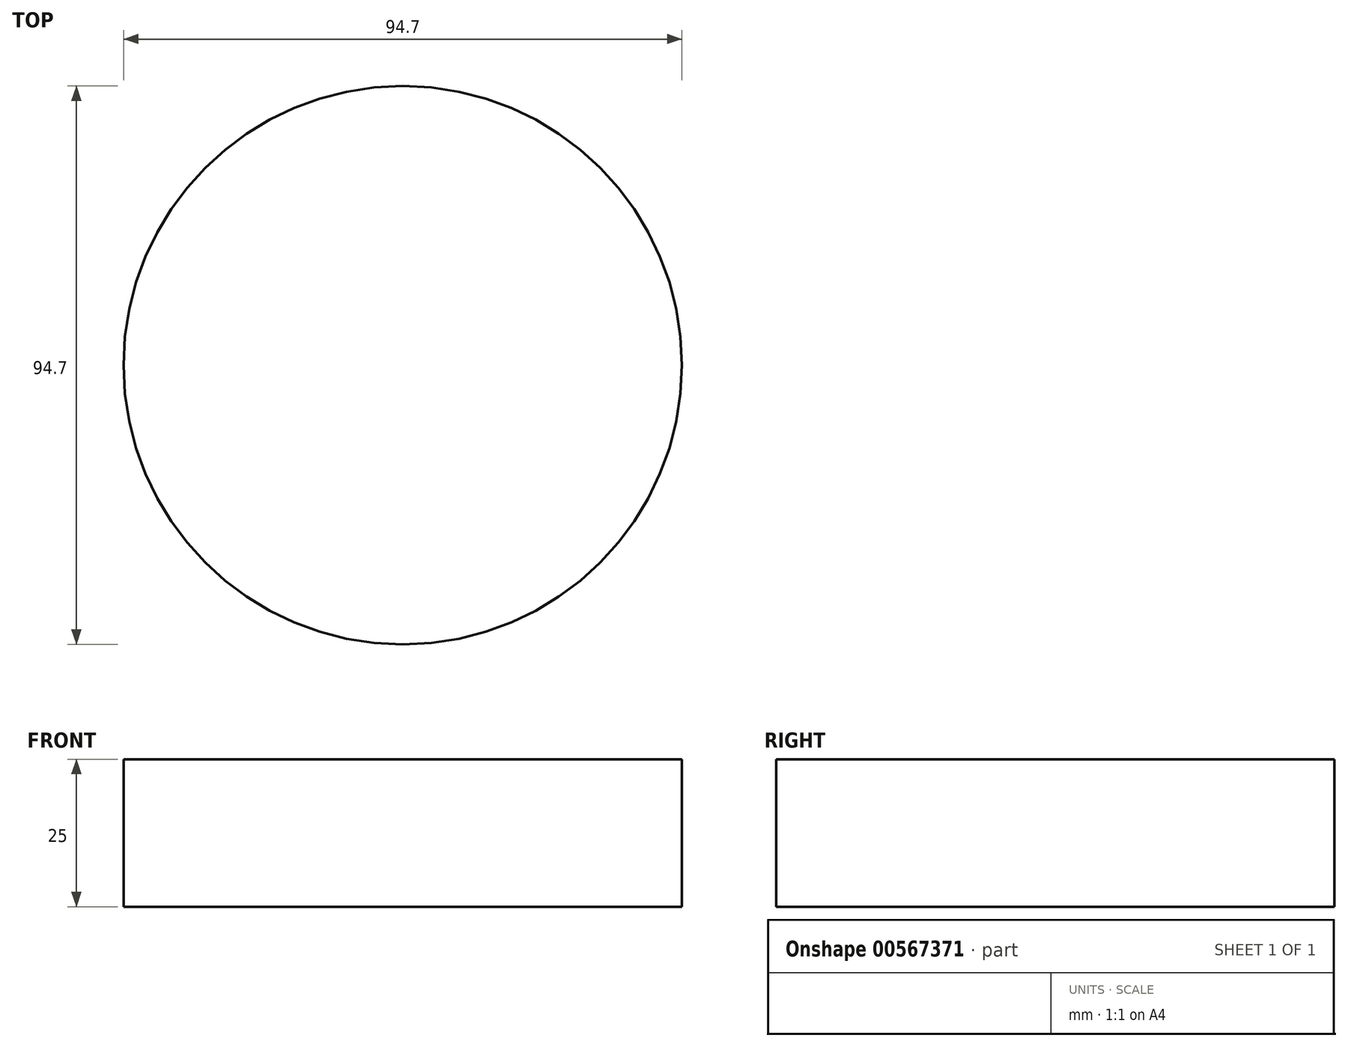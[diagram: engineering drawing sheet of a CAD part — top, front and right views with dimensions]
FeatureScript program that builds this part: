
annotation { "Feature Type Name" : "Feature", "Feature Type Description" : "" }
export const myFeature = defineFeature(function(context is Context, id is Id, definition is map)
    precondition{}
    {
        {
            var Q0;
            Q0=qCreatedBy(makeId("Top.planeOp"),FACE);
            var sketch = newSketch(context, id + "F0", { "sketchPlane" : qUnion([Q0])});
            skCircle(sketch, "E0", {"center": v(0, 0) * mm, "radius": 47.35 * mm});
            skSolve(sketch);
        }
        {
            var Q0;
            Q0 = qSketchRegion(id + "F0", true);
            extrude(context, id + "F1", {"entities" : qUnion([Q0]), "depth" : 25 * mm, "offsetDistance" : 25 * mm});
        }
    });
